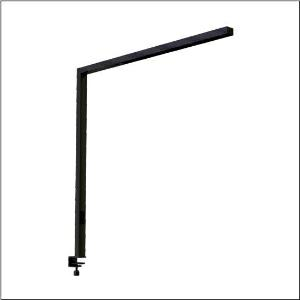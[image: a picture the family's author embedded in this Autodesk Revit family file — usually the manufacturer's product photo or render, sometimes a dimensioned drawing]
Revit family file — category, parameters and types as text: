
# Revit family: silica_r__31_desk_51my52ga4cb_9f7c
name_source: partatom
category: Lighting Fixtures
units: mm (PartAtom-declared; Revit-internal decimal feet)

## family parameters
Cut with Voids When Loaded = No
Host = Face
Light Source = No
Part Type = Normal
Room Calculation Point = No
Round Connector Dimension = Use Diameter
Shared = No

## types (1)
- Silica® 31 Desk (1 x LED, 10600 lm, 75 W, 4000K)
    Apparent Load = 75 VA
    CIE Flux Codes = 86 100 100 24 100
    Color Rendering = 80
    Color Temperature = 4000K
    Default Elevation = 1800 mm
    Description = Silica® 31 Desk, desktop luminaire, secondary optical cover: cover panel, of PMMA, light emission: direct/indirect distribution, primary light characteristic: symmetric, installation type: as desk luminaire, LED, rated luminous flux: 10.600lm, luminous efficacy: 141lm/W, light colour: 840, colour temperature: 4000K, daylight-dependent control, with cable with plug, mains connection: 230V, AC, 50Hz, connection cable pre-assembled, rated input power: 75W, luminaire head, of aluminium, jet black (RAL 9005), length: 1.203mm, width: 52mm, supporting column, angular, of aluminium, jet black (RAL 9005), baseplate, of steel, jet black (RAL 9005), protection rating (complete): IP20, insulation class (complete): insulation class I (protective earthing), certification: CE, permissible operating ambient temperature: -20..+40°C, standard: EN 50419, packaging unit: 1 piece
    Height = 36 mm
    Lamp = 1 x LED
    Lamp Light Flux = 10600 lm
    Lamp Power = 75 W
    Lamp count = 1
    Length = 1203 mm
    Luminous efficacy = 141 lm/W
    Manufacturer = Siteco
    ModVariant = No
    Model = 51MY52GA4CB
    Mounting Place = Floor
    Mounting Type = Freestanding
    Number of Poles = 1
    OnlyDefault = Yes
    Power Factor = 1
    Product Name = Silica® 31 Desk
    Product group = desktop luminaire
    ProductGroupID = 1302
    Protection Class = Protection class I
    Protection Degree = IP 20
    RLX_Detail_Level = 1
    RLX_Emergency_Light_Flux = 0 lm
    RLX_Emergency_Type = 0
    RLX_Emergency_Type_DB = No
    RlxData = <blob elided: 19129 chars, md5=c17ce8cd>
    Socket = socket
    Standby Power = 0 W
    System Light Flux = 10600 lm
    System Power = 75 W
    Type Comments = Product without accessories
    Type Image = l_1275329.jpg
    URL = http://relux.com
    VarID = ---
    Voltage = 0 V
    Weight = 0.00 kg
    Width = 52 mm  [stored 0.170604 ft]

note: [stored X ft] marks values corroborated as IEEE doubles in the binary element streams (Revit-internal decimal feet)

## geometry (parser evidence)
native form markers: Blend x4, Sweep x16
no freeform markers — native parametric forms only
